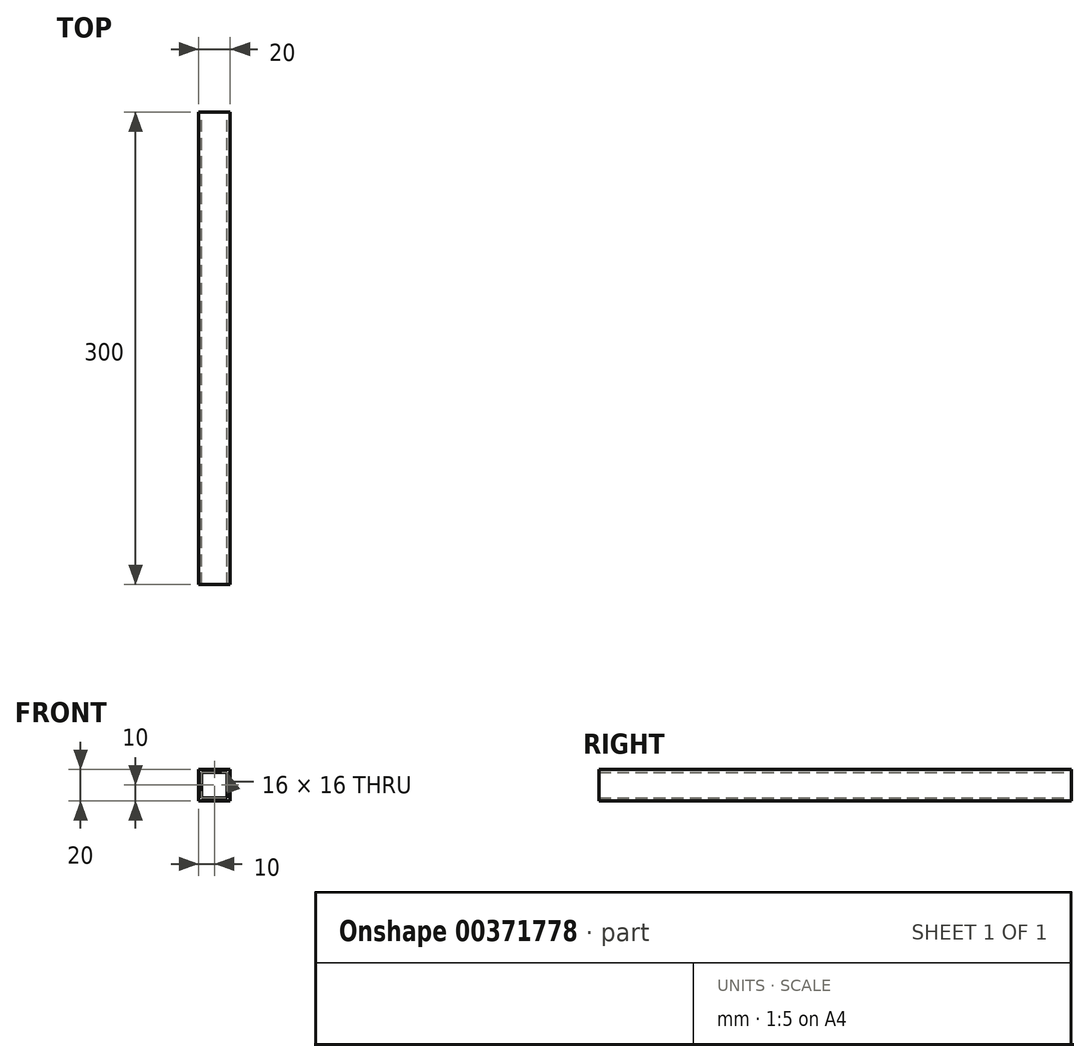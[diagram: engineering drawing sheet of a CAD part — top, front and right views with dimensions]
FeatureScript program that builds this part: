
annotation { "Feature Type Name" : "Feature", "Feature Type Description" : "" }
export const myFeature = defineFeature(function(context is Context, id is Id, definition is map)
    precondition{}
    {
        {
            var Q0;
            Q0=qCreatedBy(makeId("Front.planeOp"),FACE);
            var sketch = newSketch(context, id + "F0", { "sketchPlane" : qUnion([Q0])});
            skLineSegment(sketch, "E0.bottom", {"start": v(0, 0) * mm, "end": v(20, 0) * mm});
            skLineSegment(sketch, "E0.top", {"start": v(0, 20) * mm, "end": v(20, 20) * mm});
            skLineSegment(sketch, "E0.left", {"start": v(0, 0) * mm, "end": v(0, 20) * mm});
            skLineSegment(sketch, "E0.right", {"start": v(20, 0) * mm, "end": v(20, 20) * mm});
            skLineSegment(sketch, "E1.0", {"start": v(2, 18) * mm, "end": v(18, 18) * mm});
            skLineSegment(sketch, "E1.1", {"start": v(2, 2) * mm, "end": v(2, 18) * mm});
            skLineSegment(sketch, "E1.2", {"start": v(2, 2) * mm, "end": v(18, 2) * mm});
            skLineSegment(sketch, "E1.3", {"start": v(18, 2) * mm, "end": v(18, 18) * mm});
            skSolve(sketch);
        }
        {
            var Q0;
            Q0 = qSketchRegion(id + "F0", true);
            extrude(context, id + "F1", {"entities" : qUnion([Q0]), "depth" : 300 * mm});
        }
    });
